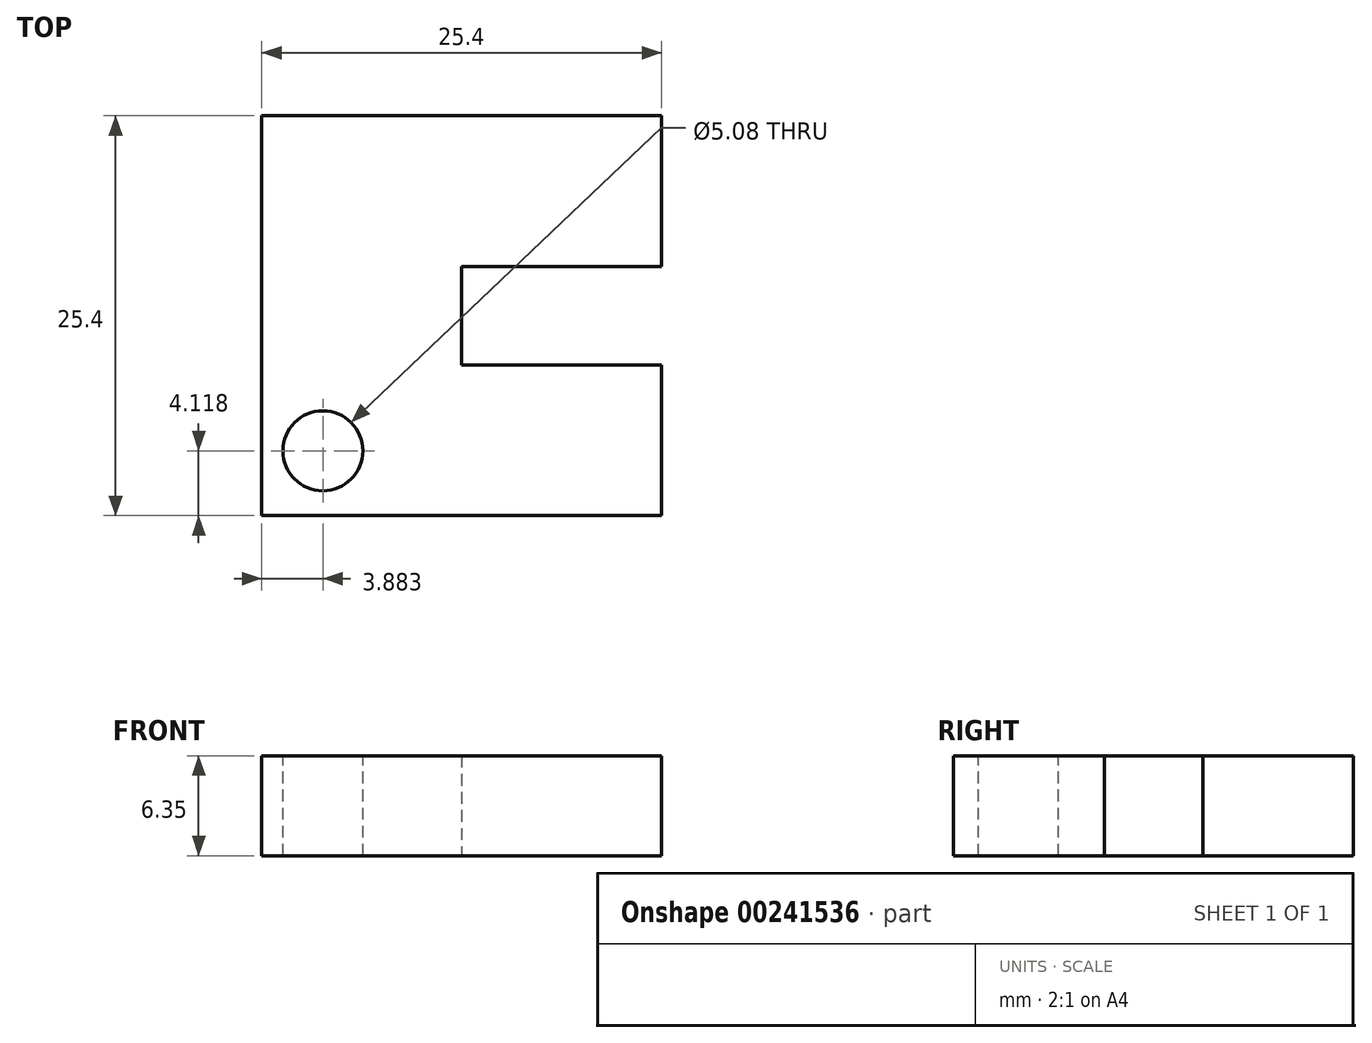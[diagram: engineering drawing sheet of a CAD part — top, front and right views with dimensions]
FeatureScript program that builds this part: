
annotation { "Feature Type Name" : "Feature", "Feature Type Description" : "" }
export const myFeature = defineFeature(function(context is Context, id is Id, definition is map)
    precondition{}
    {
        {
            var Q0;
            Q0=qCreatedBy(makeId("Top.planeOp"),FACE);
            var sketch = newSketch(context, id + "F0", { "sketchPlane" : qUnion([Q0])});
            skLineSegment(sketch, "E0", {"start": v(0, 0) * mm, "end": v(0, 25.4) * mm});
            skLineSegment(sketch, "E1", {"start": v(0, 25.4) * mm, "end": v(25.4, 25.4) * mm});
            skLineSegment(sketch, "E2", {"start": v(25.4, 25.4) * mm, "end": v(25.4, 15.84) * mm});
            skLineSegment(sketch, "E3", {"start": v(25.4, 15.84) * mm, "end": v(12.7, 15.84) * mm});
            skLineSegment(sketch, "E4", {"start": v(12.7, 15.84) * mm, "end": v(12.7, 9.56) * mm});
            skLineSegment(sketch, "E5", {"start": v(12.7, 9.56) * mm, "end": v(25.4, 9.56) * mm});
            skLineSegment(sketch, "E6", {"start": v(25.4, 9.56) * mm, "end": v(25.4, 0) * mm});
            skLineSegment(sketch, "E7", {"start": v(25.4, 0) * mm, "end": v(0, 0) * mm});
            skSolve(sketch);
        }
        {
            var Q0;
            Q0=makeQuery(id+"F0.imprint","IMPRINT",FACE,{"disambiguationData":[TD([[makeQuery(id+"F0.imprint","IMPRINT",EDGE,{"derivedFrom":sQuery(id+"F0.wireOp",EDGE,"E0")}),-1.0]])]});
            extrude(context, id + "F1", {"entities" : qUnion([Q0]), "depth" : 6.35 * mm});
        }
        {
            var Q0;
            Q0=makeQuery(id+"F1.opExtrude","CAP_FACE",FACE,{"disambiguationData":[OSD([sQuery(id+"F0.wireOp",EDGE,"E0"),sQuery(id+"F0.wireOp",EDGE,"E1"),sQuery(id+"F0.wireOp",EDGE,"E2"),sQuery(id+"F0.wireOp",EDGE,"E3"),sQuery(id+"F0.wireOp",EDGE,"E4"),sQuery(id+"F0.wireOp",EDGE,"E5"),sQuery(id+"F0.wireOp",EDGE,"E6"),sQuery(id+"F0.wireOp",EDGE,"E7")])],"isStart":false});
            var sketch = newSketch(context, id + "F2", { "sketchPlane" : qUnion([Q0])});
            skCircle(sketch, "E8", {"center": v(3.88, 4.12) * mm, "radius": 2.54 * mm});
            skSolve(sketch);
        }
        {
            var Q0;
            Q0=makeQuery(id+"F2.imprint","IMPRINT",FACE,{"disambiguationData":[TD([[makeQuery(id+"F2.imprint","IMPRINT",EDGE,{"derivedFrom":sQuery(id+"F2.wireOp",EDGE,"E8")}),1.0]])]});
            var Q1;
            Q1=sQuery(id+"F2.wireOp",EDGE,"E8");
            extrude(context, id + "F3", {"entities" : qUnion([Q0]), "operationType" : NewBodyOperationType.REMOVE, "surfaceEntities" : qUnion([Q1]), "endBound" : BoundingType.THROUGH_ALL, "oppositeDirection" : true, "depth" : 25.4 * mm});
        }
    });
